# Revit family: ledwall-mounted-e2_rd275-22w-ble2-em3_715000008800
name_source: partatom
category: Lighting Fixtures
units: mm (PartAtom-declared; Revit-internal decimal feet)

## family parameters
Cut with Voids When Loaded = No
Host = Face
Light Source = No
Part Type = Normal
Room Calculation Point = No
Round Connector Dimension = Use Diameter
Shared = No

## types (1)
- LEDWall-Mounted-E2 Rd275-22W-BLE2-EM3 (1 x LED, 2500 lm, 4000)
    Apparent Load = 22 VA
    Approval mark = CE, ENEC
    CIE Flux Codes = 44 74 93 97 100
    Color Rendering = 80
    Color Temperature = 4000
    Control Gear = Electronic ballast
    Default Elevation = 1800 mm
    Description = Stylish, compact and sturdy wall mounted fixture (IP54+IK08). Easy wiring with through-wiring possibility. Integrated CCT switch for color selection (3000K-4000K).
    Frequency = 60 Hz
    Height = 71 mm
    Lamp = 1 x LED
    Lamp Light Flux = 2500 lm
    Lamp count = 1
    Length = 275 mm
    Luminous efficacy = 114 lm/W
    Manufacturer = OPPLE
    ModVariant = No
    Model = 715000008800
    Mounting Place = Wall, Pole
    Mounting Type = Surface mounted
    Number of Poles = 1
    OnlyDefault = Yes
    Power Factor = 1
    Product Name = LEDWall-Mounted-E2 Rd275-22W-BLE2-EM3
    Product group = Wall-Mounted EcoMax G2
    ProductGroupID = 2021
    Protection Class = Protection class II
    Protection Degree = IP 54
    RLX_Detail_Level = 1
    RlxData = <blob elided: 133561 chars, md5=2f0799f1>
    Socket = socket
    Standby Power = 0 W
    System Light Flux = 2500 lm
    System Power = 22 W
    Type Comments = Product without accessories
    Type Image = web_walleco2.jpg
    URL = http://relux.com
    VarID = ---
    Voltage = 230 V
    Voltage Range = 220-240 V
    Weight = 0.00 kg
    Width = 275 mm

## geometry (parser evidence)
native form markers: Blend x4, Sweep x13
no freeform markers — native parametric forms only
